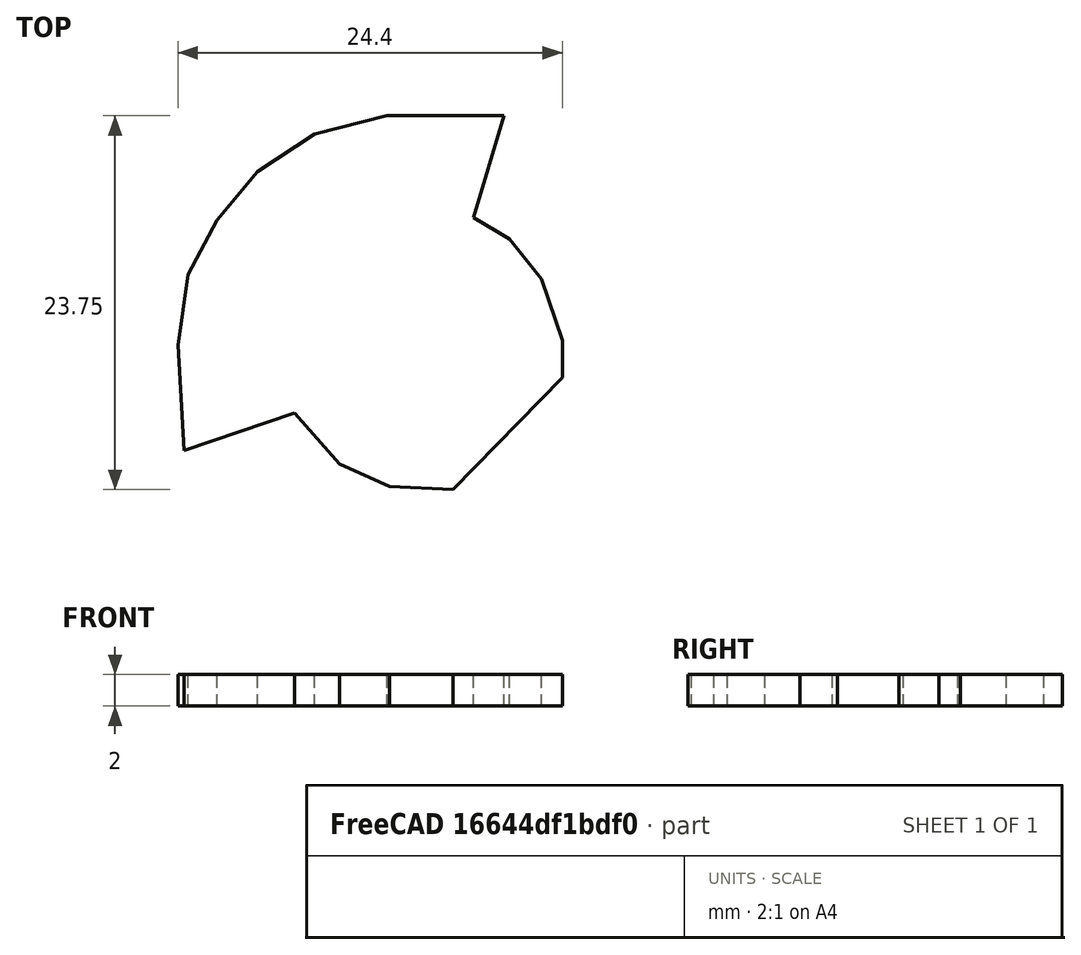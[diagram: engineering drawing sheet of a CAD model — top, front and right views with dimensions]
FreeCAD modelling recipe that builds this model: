
FCSTD DOCUMENT  (FreeCAD 0.22R35329 (Git))
Label: drill stand heat insert feet
License: All rights reserved
LicenseURL: https://en.wikipedia.org/wiki/All_rights_reserved
objects: Image::ImagePlane×1, Sketcher::SketchObject×1, PartDesign::Pad×1, PartDesign::Body×1
note: 4 computed .brp shape members not serialized (recipe doc carries the construction recipe); baked Part::Feature solids carry a one-line shape summary decoded from their .brp

FEATURE [Image::ImagePlane] _0231209_152507  label="20231209_152507"
  XSize = 201.334
  YSize = 151.001
FEATURE [Sketcher::SketchObject] Sketch
  FullyConstrained = false
  MapMode = 5
  Support = -> [XY_Plane]
  sketch-geometry (18):
    g0: LineSegment StartX=-24.9998 StartY=-1.40033 StartZ=0 EndX=-25.3726 EndY=5.27449 EndZ=0
    g1: LineSegment StartX=-25.3726 StartY=5.27449 StartZ=0 EndX=-24.7423 EndY=9.77949 EndZ=0
    g2: LineSegment StartX=-24.7423 StartY=9.77949 StartZ=0 EndX=-22.8822 EndY=13.2225 EndZ=0
    g3: LineSegment StartX=-22.8822 StartY=13.2225 StartZ=0 EndX=-20.335 EndY=16.3069 EndZ=0
    g4: LineSegment StartX=-20.335 StartY=16.3069 StartZ=0 EndX=-16.6908 EndY=18.6787 EndZ=0
    g5: LineSegment StartX=-16.6908 StartY=18.6787 StartZ=0 EndX=-12.0964 EndY=19.8542 EndZ=0
    g6: LineSegment StartX=-12.0964 StartY=19.8542 StartZ=0 EndX=-8.70097 EndY=19.8542 EndZ=0
    g7: LineSegment StartX=-8.70097 StartY=19.8542 StartZ=0 EndX=-4.68194 EndY=19.8542 EndZ=0
    g8: LineSegment StartX=-4.68194 StartY=19.8542 StartZ=0 EndX=-6.59115 EndY=13.3735 EndZ=0
    g9: LineSegment StartX=-6.59115 StartY=13.3735 StartZ=0 EndX=-4.32667 EndY=12.0167 EndZ=0
    g10: LineSegment StartX=-4.32667 StartY=12.0167 StartZ=0 EndX=-2.28996 EndY=9.48269 EndZ=0
    g11: LineSegment StartX=-2.28996 StartY=9.48269 StartZ=0 EndX=-0.969563 EndY=5.57106 EndZ=0
    g12: LineSegment StartX=-0.969563 StartY=5.57106 StartZ=0 EndX=-0.969563 EndY=3.20986 EndZ=0
    g13: LineSegment StartX=-0.969563 StartY=3.20986 StartZ=0 EndX=-7.92169 EndY=-3.90184 EndZ=0
    g14: LineSegment StartX=-7.92169 StartY=-3.90184 StartZ=0 EndX=-11.9384 EndY=-3.69738 EndZ=0
    g15: LineSegment StartX=-11.9384 StartY=-3.69738 StartZ=0 EndX=-15.1025 EndY=-2.25645 EndZ=0
    g16: LineSegment StartX=-15.1025 StartY=-2.25645 StartZ=0 EndX=-17.9591 EndY=0.985588 EndZ=0
    g17: LineSegment StartX=-17.9591 StartY=0.985588 StartZ=0 EndX=-24.9998 EndY=-1.40033 EndZ=0
  constraints (21):
    c: Coincident(g0,g1)
    c: Coincident(g1,g2)
    c: Coincident(g2,g3)
    c: Coincident(g3,g4)
    c: Coincident(g4,g5)
    c: Coincident(g5,g6)
    c: Horizontal(g6)
    c: Coincident(g6,g7)
    c: Horizontal(g7)
    c: Coincident(g7,g8)
    c: Coincident(g8,g9)
    c: Coincident(g9,g10)
    c: Coincident(g10,g11)
    c: Coincident(g11,g12)
    c: Vertical(g12)
    c: Coincident(g12,g13)
    c: Coincident(g13,g14)
    c: Coincident(g14,g15)
    c: Coincident(g15,g16)
    c: Coincident(g16,g17)
    c: Coincident(g17,g0)
FEATURE [PartDesign::Pad] Pad
  Direction = (0,0,1)
  Length = 2
  Length2 = 10
  Profile = -> Sketch
  ReferenceAxis = -> Sketch [N_Axis]
  Type = 0
FEATURE [PartDesign::Body] Body
  Group = -> [Sketch,Pad]
  Origin = -> Origin
  Tip = -> Pad
